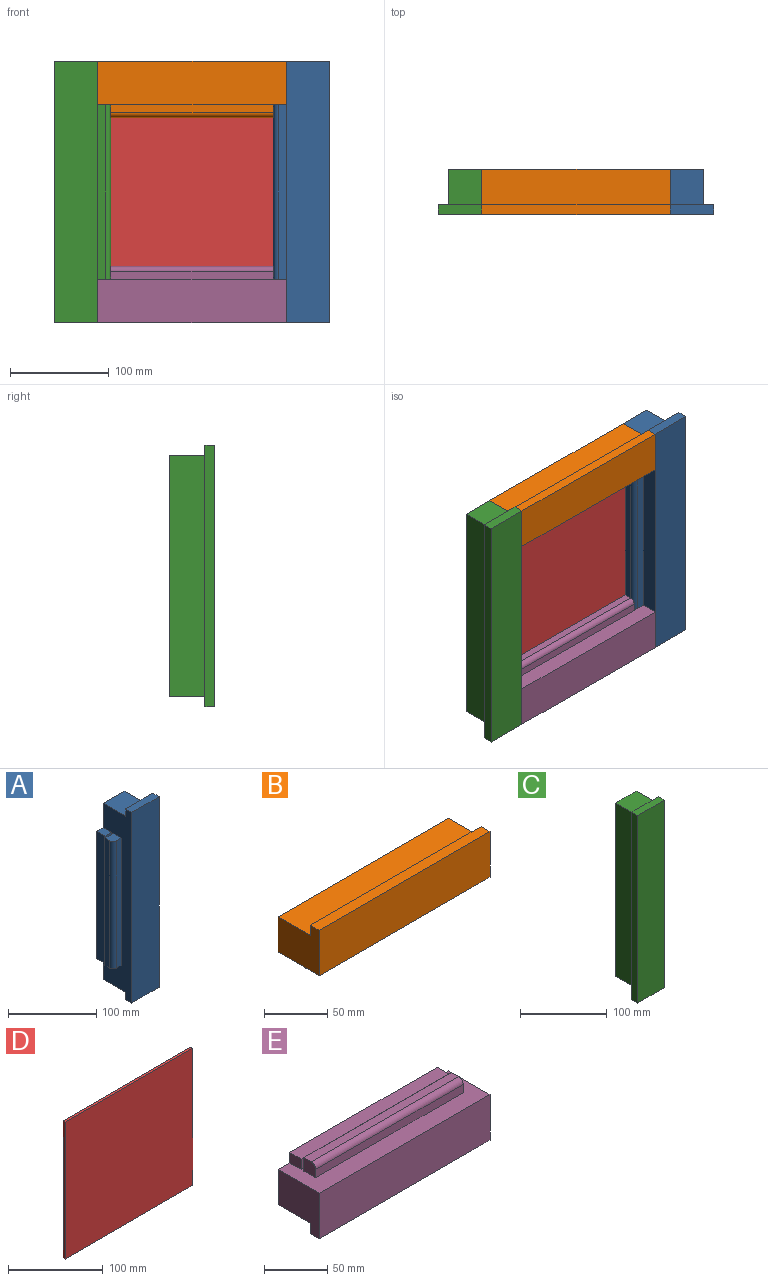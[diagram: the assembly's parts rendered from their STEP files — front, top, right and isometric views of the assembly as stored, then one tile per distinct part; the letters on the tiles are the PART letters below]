
ASSEMBLY  parts=5 mates=12
PART A: 20 faces, bbox 57x46x265 mm
  f0: plane 177x8mm, normal (-1,0,0), area 1416mm2, adj f4,f5,f16,f17
  f1: plane 245x44mm, normal (0,1,0), area 10100mm2, adj f2,f8,f9,f14,f15,f18,f19
  f2: plane 177x13mm, normal (-1,0,0), area 2301mm2, adj f1,f3,f18,f19
  f3: plane 177x10mm, normal (0,-1,0), area 1770mm2, adj f2,f8,f18,f19
  f4: plane 177x13mm, normal (0,1,0), area 2301mm2, adj f0,f8,f16,f17
  f5: cylinder r=5mm len=177mm, axis (0,0,-1), area 1390.2mm2, adj f0,f6,f16,f17
  f6: plane 177x8mm, normal (0,-1,0), area 1416mm2, adj f5,f8,f16,f17
  f7: plane 44x10mm, normal (0,0,1), area 440mm2, adj f8,f10,f11,f12
  f8: plane 265x46mm, normal (-1,0,0), area 6868mm2, adj f1,f3,f4,f6,f7,f10,f12,f13
  f9: plane 245x36mm, normal (1,0,0), area 8820mm2, adj f1,f12,f14,f15
  f10: plane 265x44mm, normal (0,-1,0), area 11660mm2, adj f7,f8,f11,f13
  f11: plane 265x10mm, normal (1,0,0), area 2650mm2, adj f7,f10,f12,f13
  f12: plane 265x44mm, normal (0,1,0), area 3330mm2, adj f7,f8,f9,f11,f13,f14,f15
  f13: plane 44x10mm, normal (0,0,-1), area 440mm2, adj f8,f10,f11,f12
  f14: plane 36x34mm, normal (0,0,-1), area 1224mm2, adj f1,f8,f9,f12
  f15: plane 36x34mm, normal (0,0,1), area 1224mm2, adj f1,f8,f9,f12
  f16: plane 13x13mm, normal (0,0,-1), area 163.6mm2, adj f0,f4,f5,f6,f8
  f17: plane 13x13mm, normal (0,0,1), area 163.6mm2, adj f0,f4,f5,f6,f8
  f18: plane 13x10mm, normal (0,0,-1), area 130mm2, adj f1,f2,f3,f8
  f19: plane 13x10mm, normal (0,0,1), area 130mm2, adj f1,f2,f3,f8
PART B: 18 faces, bbox 191x46x57 mm
  f0: plane 165x10mm, normal (0,-1,0), area 1650mm2, adj f1,f11,f16,f17
  f1: plane 165x13mm, normal (0,0,-1), area 2145mm2, adj f0,f2,f16,f17
  f2: plane 191x44mm, normal (0,1,0), area 8144mm2, adj f1,f7,f11,f12,f13,f16,f17
  f3: plane 165x8mm, normal (0,0,-1), area 1320mm2, adj f5,f6,f14,f15
  f4: plane 165x8mm, normal (0,-1,0), area 1320mm2, adj f5,f11,f14,f15
  f5: cylinder r=5mm len=165mm, axis (-1,0,0), area 1295.9mm2, adj f3,f4,f14,f15
  f6: plane 165x13mm, normal (0,1,0), area 2145mm2, adj f3,f11,f14,f15
  f7: plane 191x36mm, normal (0,0,1), area 6876mm2, adj f2,f8,f12,f13
  f8: plane 191x10mm, normal (0,1,0), area 1910mm2, adj f7,f9,f12,f13
  f9: plane 191x10mm, normal (0,0,1), area 1910mm2, adj f8,f10,f12,f13
  f10: plane 191x44mm, normal (0,-1,0), area 8404mm2, adj f9,f11,f12,f13
  f11: plane 191x46mm, normal (0,0,-1), area 4496mm2, adj f0,f2,f4,f6,f10,f12,f13,f14
  f12: plane 46x44mm, normal (1,0,0), area 1664mm2, adj f2,f7,f8,f9,f10,f11
  f13: plane 46x44mm, normal (-1,0,0), area 1664mm2, adj f2,f7,f8,f9,f10,f11
  f14: plane 13x13mm, normal (1,0,0), area 163.6mm2, adj f3,f4,f5,f6,f11
  f15: plane 13x13mm, normal (-1,0,0), area 163.6mm2, adj f3,f4,f5,f6,f11
  f16: plane 13x10mm, normal (1,0,0), area 130mm2, adj f0,f1,f2,f11
  f17: plane 13x10mm, normal (-1,0,0), area 130mm2, adj f0,f1,f2,f11
PART C: 20 faces, bbox 57x46x265 mm
  f0: plane 177x8mm, normal (1,0,0), area 1416mm2, adj f3,f4,f18,f19
  f1: plane 245x44mm, normal (0,1,0), area 10100mm2, adj f6,f7,f8,f10,f11,f16,f17
  f2: plane 177x8mm, normal (0,-1,0), area 1416mm2, adj f3,f10,f18,f19
  f3: cylinder r=5mm len=177mm, axis (0,0,-1), area 1390.2mm2, adj f0,f2,f18,f19
  f4: plane 177x13mm, normal (0,1,0), area 2301mm2, adj f0,f10,f18,f19
  f5: plane 177x10mm, normal (0,-1,0), area 1770mm2, adj f6,f10,f16,f17
  f6: plane 177x13mm, normal (1,0,0), area 2301mm2, adj f1,f5,f16,f17
  f7: plane 36x34mm, normal (0,0,-1), area 1224mm2, adj f1,f10,f11,f15
  f8: plane 36x34mm, normal (0,0,1), area 1224mm2, adj f1,f10,f11,f15
  f9: plane 44x10mm, normal (0,0,1), area 440mm2, adj f10,f12,f13,f15
  f10: plane 265x46mm, normal (1,0,0), area 6868mm2, adj f1,f2,f4,f5,f7,f8,f9,f13
  f11: plane 245x36mm, normal (-1,0,0), area 8820mm2, adj f1,f7,f8,f15
  f12: plane 265x10mm, normal (-1,0,0), area 2650mm2, adj f9,f13,f14,f15
  f13: plane 265x44mm, normal (0,-1,0), area 11660mm2, adj f9,f10,f12,f14
  f14: plane 44x10mm, normal (0,0,-1), area 440mm2, adj f10,f12,f13,f15
  f15: plane 265x44mm, normal (0,1,0), area 3330mm2, adj f7,f8,f9,f10,f11,f12,f14
  f16: plane 13x10mm, normal (0,0,1), area 130mm2, adj f1,f5,f6,f10
  f17: plane 13x10mm, normal (0,0,-1), area 130mm2, adj f1,f5,f6,f10
  f18: plane 13x13mm, normal (0,0,1), area 163.6mm2, adj f0,f2,f3,f4,f10
  f19: plane 13x13mm, normal (0,0,-1), area 163.6mm2, adj f0,f2,f3,f4,f10
PART D: 6 faces, bbox 191x3x177 mm
  f0: plane 191x3mm, normal (0,0,-1), area 573mm2, adj f1,f3,f4,f5
  f1: plane 177x3mm, normal (1,0,0), area 531mm2, adj f0,f2,f4,f5
  f2: plane 191x3mm, normal (0,0,1), area 573mm2, adj f1,f3,f4,f5
  f3: plane 177x3mm, normal (-1,0,0), area 531mm2, adj f0,f2,f4,f5
  f4: plane 191x177mm, normal (0,-1,0), area 33807mm2, adj f0,f1,f2,f3
  f5: plane 191x177mm, normal (0,1,0), area 33807mm2, adj f0,f1,f2,f3
PART E: 18 faces, bbox 191x46x57 mm
  f0: plane 46x44mm, normal (1,0,0), area 1664mm2, adj f2,f9,f10,f11,f12,f13
  f1: plane 46x44mm, normal (-1,0,0), area 1664mm2, adj f2,f9,f10,f11,f12,f13
  f2: plane 191x44mm, normal (0,1,0), area 8144mm2, adj f0,f1,f3,f9,f13,f16,f17
  f3: plane 165x13mm, normal (0,0,1), area 2145mm2, adj f2,f4,f16,f17
  f4: plane 165x10mm, normal (0,-1,0), area 1650mm2, adj f3,f9,f16,f17
  f5: plane 165x8mm, normal (0,0,1), area 1320mm2, adj f6,f7,f14,f15
  f6: plane 165x13mm, normal (0,1,0), area 2145mm2, adj f5,f9,f14,f15
  f7: cylinder r=5mm len=165mm, axis (-1,0,0), area 1295.9mm2, adj f5,f8,f14,f15
  f8: plane 165x8mm, normal (0,-1,0), area 1320mm2, adj f7,f9,f14,f15
  f9: plane 191x46mm, normal (0,0,1), area 4496mm2, adj f0,f1,f2,f4,f6,f8,f10,f14
  f10: plane 191x44mm, normal (0,-1,0), area 8404mm2, adj f0,f1,f9,f11
  f11: plane 191x10mm, normal (0,0,-1), area 1910mm2, adj f0,f1,f10,f12
  f12: plane 191x10mm, normal (0,1,0), area 1910mm2, adj f0,f1,f11,f13
  f13: plane 191x36mm, normal (0,0,-1), area 6876mm2, adj f0,f1,f2,f12
  f14: plane 13x13mm, normal (1,0,0), area 163.6mm2, adj f5,f6,f7,f8,f9
  f15: plane 13x13mm, normal (-1,0,0), area 163.6mm2, adj f5,f6,f7,f8,f9
  f16: plane 13x10mm, normal (-1,0,0), area 130mm2, adj f2,f3,f4,f9
  f17: plane 13x10mm, normal (1,0,0), area 130mm2, adj f2,f3,f4,f9
PLACE A t=(13,-18.28,0)mm
PLACE B t=(13,-18.28,0)mm
PLACE C t=(13,-18.28,0)mm
PLACE D t=(13,-18.28,0)mm
PLACE E t=(13,-18.28,0)mm
MATE planar A.f14 <-> E.f13  axis (0,0,-1) through (125.5,9.72,10)mm
MATE planar A.f10 <-> E.f10  axis (0,-1,0) through (130.5,-18.28,132.5)mm
MATE planar C.f13 <-> E.f10  axis (0,-1,0) through (-104.5,-18.28,132.5)mm
MATE planar B.f13 <-> C.f10  axis (-1,0,0) through (-82.5,3.64,239.32)mm
MATE planar B.f10 <-> C.f13  axis (0,-1,0) through (13,-18.28,243)mm
MATE planar D.f1 <-> E.f0  axis (1,0,0) through (108.5,13.22,132.5)mm
MATE planar C.f7 <-> E.f13  axis (0,0,-1) through (-99.5,9.72,10)mm
MATE planar B.f7 <-> C.f8  axis (0,0,1) through (-82.5,-8.28,255)mm
MATE planar C.f10 <-> E.f1  axis (1,0,0) through (-82.5,-8.28,255)mm
MATE planar D.f5 <-> E.f4  axis (0,1,0) through (13,14.72,132.5)mm
MATE planar D.f0 <-> E.f9  axis (0,0,-1) through (13,13.22,44)mm
MATE planar A.f8 <-> E.f0  axis (-1,0,0) through (108.5,-1.5,132.5)mm
